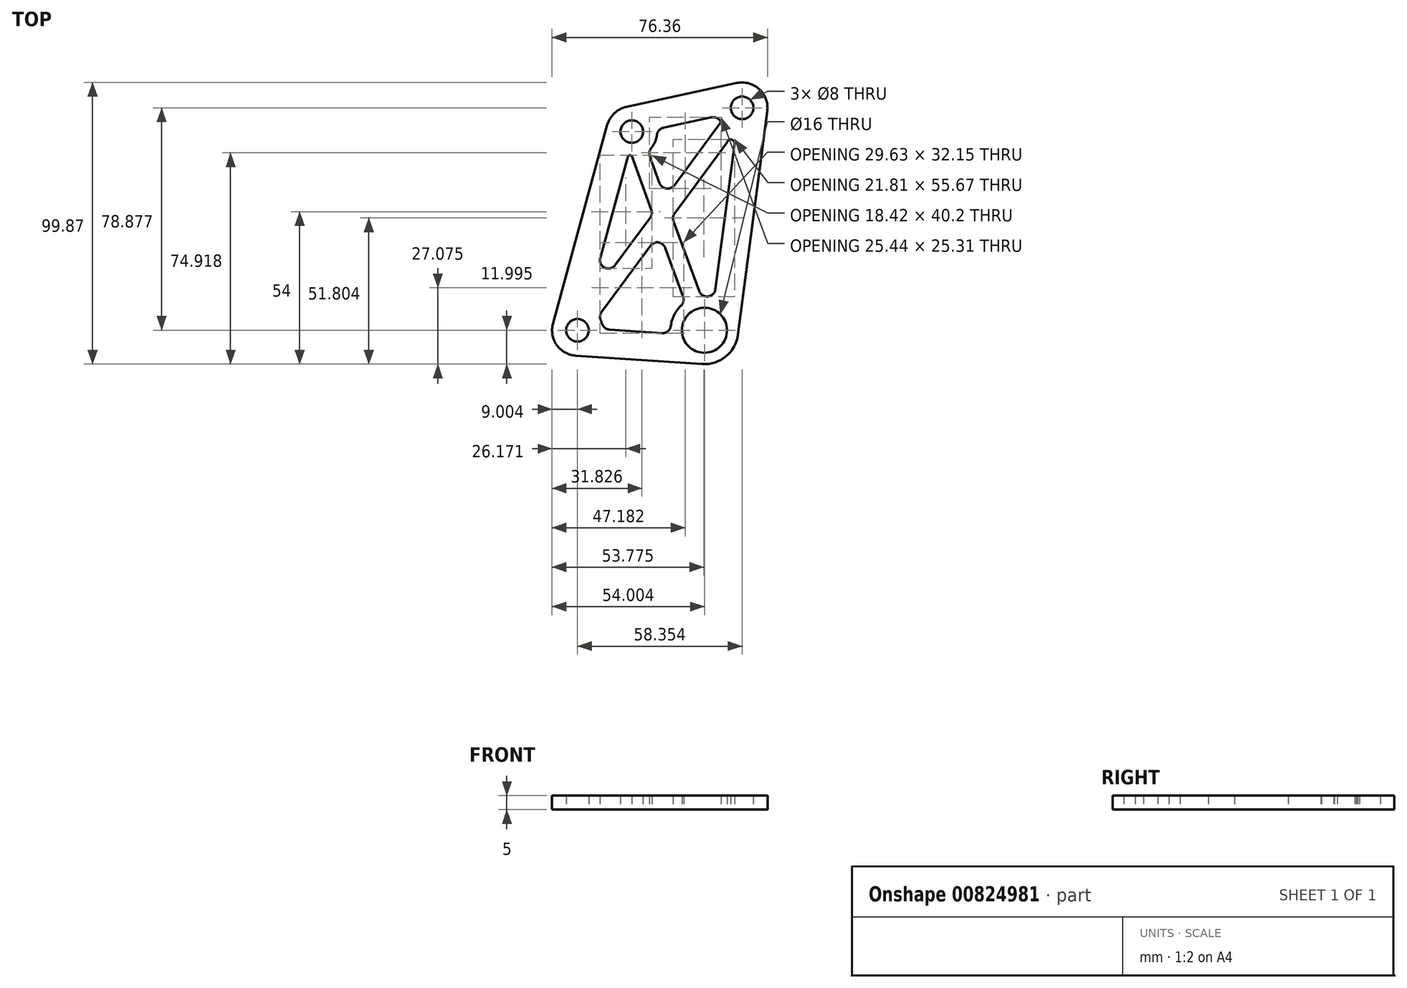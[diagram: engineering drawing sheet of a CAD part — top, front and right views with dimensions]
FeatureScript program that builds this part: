
annotation { "Feature Type Name" : "Feature", "Feature Type Description" : "" }
export const myFeature = defineFeature(function(context is Context, id is Id, definition is map)
    precondition{}
    {
        {
            var Q0;
            Q0=qCreatedBy(makeId("Top.planeOp"),FACE);
            var sketch = newSketch(context, id + "F0", { "sketchPlane" : qUnion([Q0])});
            skCircle(sketch, "E0", {"center": v(7.93, -14.4) * mm, "radius": 8 * mm});
            skCircle(sketch, "E1", {"center": v(-37.07, -14.4) * mm, "radius": 4 * mm});
            skCircle(sketch, "E2", {"center": v(21.29, 64.48) * mm, "radius": 4 * mm});
            skCircle(sketch, "E3", {"center": v(-17.81, 56.05) * mm, "radius": 4 * mm});
            skLineSegment(sketch, "E4", {"start": v(21.29, 64.48) * mm, "end": v(-37.07, -14.4) * mm, "construction": true});
            skLineSegment(sketch, "E5", {"start": v(-17.81, 56.05) * mm, "end": v(7.93, -14.4) * mm, "construction": true});
            skLineSegment(sketch, "E6", {"start": v(21.29, 64.48) * mm, "end": v(7.93, -14.4) * mm, "construction": true});
            skLineSegment(sketch, "E7", {"start": v(-37.07, -14.4) * mm, "end": v(7.93, -14.4) * mm, "construction": true});
            skLineSegment(sketch, "E8", {"start": v(-17.81, 56.05) * mm, "end": v(-37.07, -14.4) * mm, "construction": true});
            skLineSegment(sketch, "E9", {"start": v(-17.81, 56.05) * mm, "end": v(21.29, 64.48) * mm, "construction": true});
            skArc(sketch, "E10", {"start": v(-28.4, -11.97) * mm, "mid": v(-28.59, -11.38) * mm, "end": v(-28.81, -10.8) * mm});
            skArc(sketch, "E11", {"start": v(-19.71, 64.85) * mm, "mid": v(-24, 62.58) * mm, "end": v(-26.5, 58.42) * mm});
            skArc(sketch, "E12", {"start": v(30.21, 63.31) * mm, "mid": v(27.39, 71.1) * mm, "end": v(19.4, 73.28) * mm});
            skArc(sketch, "E13", {"start": v(8.7, -2.42) * mm, "mid": v(8.68, -2.42) * mm, "end": v(8.67, -2.42) * mm});
            skLineSegment(sketch, "E14", {"start": v(30.21, 63.31) * mm, "end": v(19.83, -15.95) * mm});
            skLineSegment(sketch, "E15", {"start": v(-37.67, -23.37) * mm, "end": v(7.13, -26.37) * mm});
            skLineSegment(sketch, "E16", {"start": v(-45.75, -12.02) * mm, "end": v(-26.5, 58.42) * mm});
            skLineSegment(sketch, "E17", {"start": v(-19.71, 64.85) * mm, "end": v(19.4, 73.28) * mm});
            skLineSegment(sketch, "E18", {"start": v(18.61, 51.75) * mm, "end": v(11.86, 0.19) * mm});
            skLineSegment(sketch, "E19", {"start": v(-25.71, -14.15) * mm, "end": v(-7.13, -15.4) * mm});
            skLineSegment(sketch, "E20", {"start": v(-29.01, 11.29) * mm, "end": v(-19.2, 47.16) * mm});
            skLineSegment(sketch, "E21", {"start": v(10.44, 61.12) * mm, "end": v(-6.54, 57.46) * mm});
            skArc(sketch, "E22.trimOffspring", {"start": v(13.63, 59.76) * mm, "mid": v(13.73, 59.6) * mm, "end": v(13.83, 59.45) * mm});
            skArc(sketch, "E23.trimOffspring", {"start": v(7.13, -26.37) * mm, "mid": v(15.54, -23.67) * mm, "end": v(19.83, -15.95) * mm});
            skArc(sketch, "E24.trimOffspring", {"start": v(-45.75, -12.02) * mm, "mid": v(-44.4, -19.61) * mm, "end": v(-37.67, -23.37) * mm});
            skLineSegment(sketch, "E25", {"start": v(-11.43, 47.32) * mm, "end": v(-7.96, 37.82) * mm});
            skLineSegment(sketch, "E26", {"start": v(-17.72, 47.05) * mm, "end": v(-10.87, 28.32) * mm});
            skLineSegment(sketch, "E27", {"start": v(-23.7, 8.7) * mm, "end": v(-11.28, 25.5) * mm});
            skLineSegment(sketch, "E28.trimOffspring", {"start": v(-11.17, 15.57) * mm, "end": v(-28.47, -7.82) * mm});
            skLineSegment(sketch, "E29.trimOffspring", {"start": v(-5.94, 14.82) * mm, "end": v(0.4, -2.51) * mm});
            skLineSegment(sketch, "E30.trimOffspring", {"start": v(-2.73, 37.07) * mm, "end": v(13.83, 59.45) * mm});
            skLineSegment(sketch, "E31.trimOffspring", {"start": v(-3.02, 24.32) * mm, "end": v(6.03, -0.45) * mm});
            skArc(sketch, "E32.trimOffspring", {"start": v(-0.35, -5.71) * mm, "mid": v(-2.76, -8.95) * mm, "end": v(-3.96, -12.8) * mm});
            skArc(sketch, "E33.trimOffspring", {"start": v(-33.74, -6.03) * mm, "mid": v(-34.21, -5.86) * mm, "end": v(-34.7, -5.71) * mm});
            skArc(sketch, "E34.trimOffspring", {"start": v(-10.91, 50.27) * mm, "mid": v(-9.57, 52.44) * mm, "end": v(-8.89, 54.9) * mm});
            skPoint(sketch, "E35.visualSharp", {"position": v(-6.04, 32.58) * mm});
            skArc(sketch, "E35.filletArc", {"start": v(-7.96, 37.82) * mm, "mid": v(-5.57, 35.88) * mm, "end": v(-2.73, 37.07) * mm});
            skPoint(sketch, "E36.visualSharp", {"position": v(-10.32, 26.8) * mm});
            skArc(sketch, "E36.filletArc", {"start": v(-11.28, 25.5) * mm, "mid": v(-10.72, 26.86) * mm, "end": v(-10.87, 28.32) * mm});
            skPoint(sketch, "E37.visualSharp", {"position": v(-3.57, 25.83) * mm});
            skArc(sketch, "E37.filletArc", {"start": v(-2.61, 27.13) * mm, "mid": v(-3.17, 25.77) * mm, "end": v(-3.02, 24.32) * mm});
            skPoint(sketch, "E38.visualSharp", {"position": v(-7.85, 20.05) * mm});
            skArc(sketch, "E38.filletArc", {"start": v(-5.94, 14.82) * mm, "mid": v(-8.33, 16.76) * mm, "end": v(-11.17, 15.57) * mm});
            skPoint(sketch, "E39.visualSharp", {"position": v(-4, -15.6) * mm});
            skArc(sketch, "E39.filletArc", {"start": v(-7.13, -15.4) * mm, "mid": v(-5.03, -14.72) * mm, "end": v(-3.96, -12.8) * mm});
            skPoint(sketch, "E40.visualSharp", {"position": v(1.13, -4.51) * mm});
            skArc(sketch, "E40.filletArc", {"start": v(-0.35, -5.71) * mm, "mid": v(0.5, -4.22) * mm, "end": v(0.4, -2.51) * mm});
            skPoint(sketch, "E41.visualSharp", {"position": v(6.76, -2.45) * mm});
            skArc(sketch, "E41.filletArc", {"start": v(6.03, -0.45) * mm, "mid": v(7.06, -1.83) * mm, "end": v(8.67, -2.42) * mm});
            skPoint(sketch, "E42.visualSharp", {"position": v(11.45, -2.92) * mm});
            skArc(sketch, "E42.filletArc", {"start": v(8.7, -2.42) * mm, "mid": v(10.8, -1.74) * mm, "end": v(11.86, 0.19) * mm});
            skPoint(sketch, "E43.visualSharp", {"position": v(-29.6, -9.36) * mm});
            skArc(sketch, "E43.filletArc", {"start": v(-28.47, -7.82) * mm, "mid": v(-29.04, -9.27) * mm, "end": v(-28.81, -10.8) * mm});
            skPoint(sketch, "E44.visualSharp", {"position": v(-33.24, -4.17) * mm});
            skArc(sketch, "E44.filletArc", {"start": v(-29.01, 11.29) * mm, "mid": v(-27.43, 7.8) * mm, "end": v(-23.7, 8.7) * mm});
            skPoint(sketch, "E45.visualSharp", {"position": v(12.76, 61.62) * mm});
            skArc(sketch, "E45.filletArc", {"start": v(13.63, 59.76) * mm, "mid": v(12.25, 60.95) * mm, "end": v(10.44, 61.12) * mm});
            skPoint(sketch, "E46.visualSharp", {"position": v(-8.86, 56.96) * mm});
            skArc(sketch, "E46.filletArc", {"start": v(-6.54, 57.46) * mm, "mid": v(-8.12, 56.55) * mm, "end": v(-8.89, 54.9) * mm});
            skPoint(sketch, "E47.visualSharp", {"position": v(-12.08, 49.1) * mm});
            skArc(sketch, "E47.filletArc", {"start": v(-10.91, 50.27) * mm, "mid": v(-11.56, 48.86) * mm, "end": v(-11.43, 47.32) * mm});
            skPoint(sketch, "E48.visualSharp", {"position": v(-28.08, -14) * mm});
            skArc(sketch, "E48.filletArc", {"start": v(-28.4, -11.97) * mm, "mid": v(-27.4, -13.49) * mm, "end": v(-25.71, -14.15) * mm});
            skLineSegment(sketch, "E49", {"start": v(-17.72, 47.05) * mm, "end": v(-17.84, 47.37) * mm});
            skArc(sketch, "E50", {"start": v(-19.2, 47.16) * mm, "mid": v(-18.6, 47.7) * mm, "end": v(-17.84, 47.37) * mm});
            skPoint(sketch, "E51", {"position": v(18.01, 55.01) * mm});
            skPoint(sketch, "E52", {"position": v(19, 54.73) * mm});
            skArc(sketch, "E53", {"start": v(18.61, 51.75) * mm, "mid": v(17.54, 53.25) * mm, "end": v(15.98, 52.26) * mm});
            skLineSegment(sketch, "E54.trimOffspring", {"start": v(15.98, 52.26) * mm, "end": v(-2.61, 27.13) * mm});
            skSolve(sketch);
        }
        {
            var Q0;
            Q0 = qSketchRegion(id + "F0", true);
            extrude(context, id + "F1", {"entities" : qUnion([Q0]), "depth" : 5 * mm, "offsetDistance" : 25.4 * mm});
        }
    });
